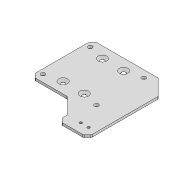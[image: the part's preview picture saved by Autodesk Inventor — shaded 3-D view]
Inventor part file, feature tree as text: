
AUTODESK INVENTOR PART (.ipt)
format: ipt  version: 2020 (Build 240168000, 168)  size: 172,544 bytes
history: native  units: mm
features: sketch x5, hole x3, extrude x2, chamfer x2, projected_geometry x2, other x1, fillet x1
ambient origin geometry x8: Origin, YZ Plane, XZ Plane, XY Plane, X Axis, Y Axis, Z Axis, Center Point
bodies: Body1 (feature_tree)
feature tree (16):
  other  "ソリッド1"
  extrude  "押し出し1"  Depth=80.0mm
  hole  "穴1"  [1 undecoded]
  hole  "穴2"  [1 undecoded]
  extrude  "押し出し2"  Depth=68.0mm
  hole  "穴3"  [1 undecoded]
  chamfer  "面取り1"  Distance=27.0mm
  chamfer  "面取り2"  Distance=50.0mm
  fillet  "フィレット3"  Radius=110.0mm
  sketch  "スケッチ1"
  sketch  "スケッチ2"
  sketch  "スケッチ3"
  sketch  "スケッチ4"
  projected_geometry  "投影ループ1"
  sketch  "スケッチ5"
  projected_geometry  "投影ループ2"
note: 3 required parameter values undecoded (feature->parameter linkage not recoverable at this tier; creation-order binding heuristic only, values carry confidence <= 0.55)
